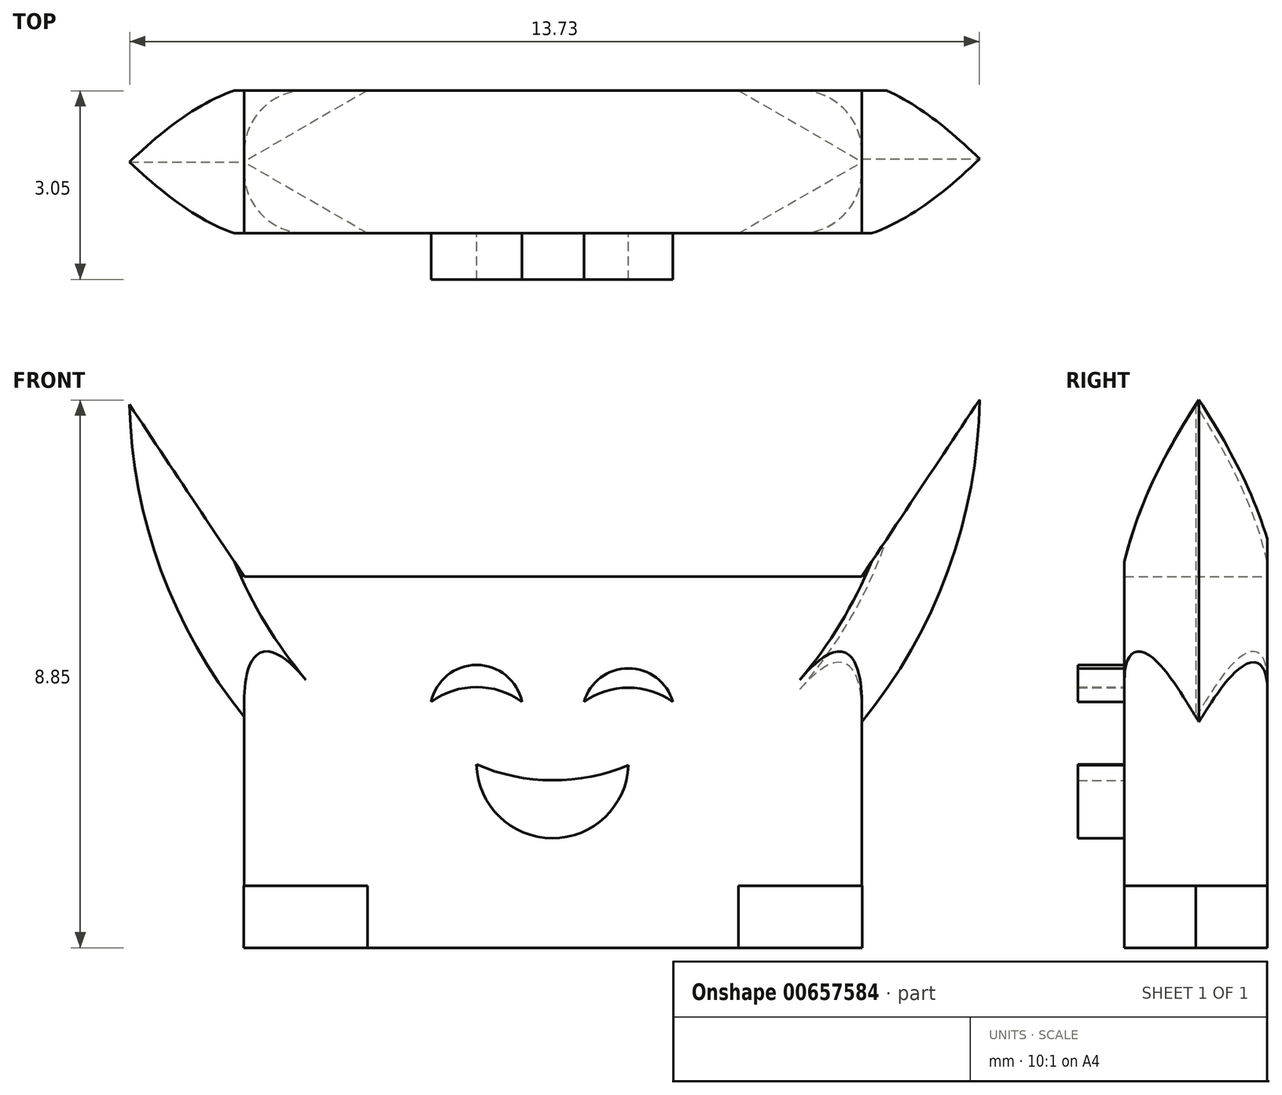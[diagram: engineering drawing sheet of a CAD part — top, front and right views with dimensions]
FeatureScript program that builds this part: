
annotation { "Feature Type Name" : "Feature", "Feature Type Description" : "" }
export const myFeature = defineFeature(function(context is Context, id is Id, definition is map)
    precondition{}
    {
        {
            var Q0;
            Q0=qCreatedBy(makeId("Top.planeOp"),FACE);
            var sketch = newSketch(context, id + "F0", { "sketchPlane" : qUnion([Q0])});
            skLineSegment(sketch, "E0.bottom", {"start": v(-3, -1.15) * mm, "end": v(3, -1.15) * mm});
            skLineSegment(sketch, "E0.top", {"start": v(-3, 1.15) * mm, "end": v(3, 1.15) * mm});
            skPoint(sketch, "E0.middle", {"position": v(0, 0) * mm});
            skLineSegment(sketch, "E1", {"start": v(-3, 1.15) * mm, "end": v(-5, 0) * mm});
            skLineSegment(sketch, "E2", {"start": v(-3, -1.15) * mm, "end": v(-5, 0) * mm});
            skLineSegment(sketch, "E3", {"start": v(3, 1.15) * mm, "end": v(5, 0) * mm});
            skLineSegment(sketch, "E4", {"start": v(3, -1.15) * mm, "end": v(5, 0) * mm});
            skSolve(sketch);
        }
        {
            var Q0;
            Q0 = qSketchRegion(id + "F0", true);
            extrude(context, id + "F1", {"entities" : qUnion([Q0]), "depth" : 1 * mm, "offsetDistance" : 25 * mm});
        }
        {
            var Q0;
            Q0=makeQuery(id+"F1.opExtrude","CAP_FACE",FACE,{"disambiguationData":[OSD([sQuery(id+"F0.wireOp",EDGE,"E0.bottom"),sQuery(id+"F0.wireOp",EDGE,"E0.top"),sQuery(id+"F0.wireOp",EDGE,"E1"),sQuery(id+"F0.wireOp",EDGE,"E2"),sQuery(id+"F0.wireOp",EDGE,"E3"),sQuery(id+"F0.wireOp",EDGE,"E4")])],"isStart":false});
            var sketch = newSketch(context, id + "F2", { "sketchPlane" : qUnion([Q0])});
            skLineSegment(sketch, "E5.bottom", {"start": v(-5, 1.15) * mm, "end": v(5, 1.15) * mm});
            skLineSegment(sketch, "E5.top", {"start": v(-5, -1.15) * mm, "end": v(5, -1.15) * mm});
            skLineSegment(sketch, "E5.left", {"start": v(-5, 1.15) * mm, "end": v(-5, -1.15) * mm});
            skLineSegment(sketch, "E5.right", {"start": v(5, 1.15) * mm, "end": v(5, -1.15) * mm});
            skPoint(sketch, "E5.middle", {"position": v(0, 0) * mm});
            skSolve(sketch);
        }
        {
            var Q0;
            Q0 = qSketchRegion(id + "F2", true);
            extrude(context, id + "F3", {"entities" : qUnion([Q0]), "operationType" : NewBodyOperationType.ADD, "depth" : 5 * mm, "offsetDistance" : 25 * mm});
        }
        {
            var Q0;
            Q0=makeQuery(id+"F3.opExtrude","SWEPT_FACE",FACE,{"disambiguationData":[OSD([sQuery(id+"F2.wireOp",EDGE,"E5.right")])]});
            var sketch = newSketch(context, id + "F4", { "sketchPlane" : qUnion([Q0])});
            skLineSegment(sketch, "E6.bottom", {"start": v(-1.15, 1) * mm, "end": v(1.15, 1) * mm});
            skLineSegment(sketch, "E6.top", {"start": v(-1.15, 3.5) * mm, "end": v(1.15, 3.5) * mm});
            skLineSegment(sketch, "E6.left", {"start": v(-1.15, 1) * mm, "end": v(-1.15, 3.5) * mm});
            skLineSegment(sketch, "E6.right", {"start": v(1.15, 1) * mm, "end": v(1.15, 3.5) * mm});
            skLineSegment(sketch, "E7.top", {"start": v(-1.15, 6) * mm, "end": v(1.15, 6) * mm});
            skLineSegment(sketch, "E7.left", {"start": v(-1.15, 3.5) * mm, "end": v(-1.15, 6) * mm});
            skLineSegment(sketch, "E7.right", {"start": v(1.15, 3.5) * mm, "end": v(1.15, 6) * mm});
            skSolve(sketch);
        }
        {
            var Q0;
            Q0=makeQuery(id+"F4.imprint","IMPRINT",FACE,{"disambiguationData":[TD([[makeQuery(id+"F4.imprint","IMPRINT",EDGE,{"derivedFrom":sQuery(id+"F4.wireOp",EDGE,"E6.top")}),1.0]])]});
            extrude(context, id + "F5", {"entities" : qUnion([Q0]), "operationType" : NewBodyOperationType.ADD, "depth" : 2 * mm, "offsetDistance" : 25 * mm});
        }
        {
            var Q0;
            Q0=makeQuery(id+"F5.boolean.opBoolean","MERGE",FACE,{"derivedFrom":[makeQuery(id+"F3.opExtrude","CAP_FACE",FACE,{"disambiguationData":[OSD([sQuery(id+"F2.wireOp",EDGE,"E5.bottom"),sQuery(id+"F2.wireOp",EDGE,"E5.top"),sQuery(id+"F2.wireOp",EDGE,"E5.left"),sQuery(id+"F2.wireOp",EDGE,"E5.right")])],"isStart":false}),makeQuery(id+"F5.opExtrude","SWEPT_FACE",FACE,{"disambiguationData":[OSD([sQuery(id+"F4.wireOp",EDGE,"E7.top")])]})]});
            var sketch = newSketch(context, id + "F6", { "sketchPlane" : qUnion([Q0])});
            skLineSegment(sketch, "E8.bottom", {"start": v(7, -1.15) * mm, "end": v(5, -1.15) * mm});
            skLineSegment(sketch, "E8.top", {"start": v(7, 1.15) * mm, "end": v(5, 1.15) * mm});
            skLineSegment(sketch, "E8.left", {"start": v(7, -1.15) * mm, "end": v(7, 1.15) * mm});
            skLineSegment(sketch, "E8.right", {"start": v(5, -1.15) * mm, "end": v(5, 1.15) * mm});
            skSolve(sketch);
        }
        {
            var Q0;
            Q0=makeQuery(id+"F6.imprint","IMPRINT",FACE,{"disambiguationData":[TD([[makeQuery(id+"F6.imprint","IMPRINT",EDGE,{"derivedFrom":sQuery(id+"F6.wireOp",EDGE,"E8.bottom")}),1.0]])]});
            extrude(context, id + "F7", {"entities" : qUnion([Q0]), "operationType" : NewBodyOperationType.ADD, "depth" : 3 * mm, "offsetDistance" : 25 * mm});
        }
        {
            var Q0;
            Q0=makeQuery(id+"F5.opExtrude","CAP_EDGE",EDGE,{"disambiguationData":[OSD([sQuery(id+"F4.wireOp",EDGE,"E6.top")])],"isStart":false});
            fillet(context, id + "F8", {"entities" : qUnion([Q0]), "radius" : 8.5 * mm, "tangentPropagation" : true, "allowEdgeOverflow" : false});
        }
        {
            var Q0;
            Q0=makeQuery(id+"F7.opExtrude","CAP_EDGE",EDGE,{"disambiguationData":[OSD([sQuery(id+"F6.wireOp",EDGE,"E8.right")])],"isStart":false});
            chamfer(context, id + "F9", {"entities" : qUnion([Q0]), "chamferType" : ChamferType.TWO_OFFSETS, "width1" : 3 * mm, "oppositeDirection" : false, "width2" : 2 * mm, "tangentPropagation" : true});
        }
        {
            var Q0;
            Q0=makeQuery(id+"F8.opFillet","BLEND_EDGE",EDGE,{"blendedFrom":[makeQuery(id+"F5.opExtrude","CAP_EDGE",EDGE,{"disambiguationData":[OSD([sQuery(id+"F4.wireOp",EDGE,"E6.top")])],"isStart":false}),makeQuery(id+"F7.boolean.opBoolean","MERGE",FACE,{"derivedFrom":[makeQuery(id+"F5.boolean.opBoolean","MERGE",FACE,{"derivedFrom":[makeQuery(id+"F3.boolean.opBoolean","MERGE",FACE,{"derivedFrom":[makeQuery(id+"F1.opExtrude","SWEPT_FACE",FACE,{"disambiguationData":[OSD([sQuery(id+"F0.wireOp",EDGE,"E0.bottom")])]}),makeQuery(id+"F3.opExtrude","SWEPT_FACE",FACE,{"disambiguationData":[OSD([sQuery(id+"F2.wireOp",EDGE,"E5.top")])]})]}),makeQuery(id+"F5.opExtrude","SWEPT_FACE",FACE,{"disambiguationData":[OSD([sQuery(id+"F4.wireOp",EDGE,"E7.left")])]})]}),makeQuery(id+"F7.opExtrude","SWEPT_FACE",FACE,{"disambiguationData":[OSD([sQuery(id+"F6.wireOp",EDGE,"E8.bottom")])]})]})],"blendedInto":[makeQuery(id+"F7.boolean.opBoolean","MERGE",FACE,{"derivedFrom":[makeQuery(id+"F5.boolean.opBoolean","MERGE",FACE,{"derivedFrom":[makeQuery(id+"F3.boolean.opBoolean","MERGE",FACE,{"derivedFrom":[makeQuery(id+"F1.opExtrude","SWEPT_FACE",FACE,{"disambiguationData":[OSD([sQuery(id+"F0.wireOp",EDGE,"E0.bottom")])]}),makeQuery(id+"F3.opExtrude","SWEPT_FACE",FACE,{"disambiguationData":[OSD([sQuery(id+"F2.wireOp",EDGE,"E5.top")])]})]}),makeQuery(id+"F5.opExtrude","SWEPT_FACE",FACE,{"disambiguationData":[OSD([sQuery(id+"F4.wireOp",EDGE,"E7.left")])]})]}),makeQuery(id+"F7.opExtrude","SWEPT_FACE",FACE,{"disambiguationData":[OSD([sQuery(id+"F6.wireOp",EDGE,"E8.bottom")])]})]})]});
            chamfer(context, id + "F10", {"entities" : qUnion([Q0]), "width" : 1.3 * mm, "tangentPropagation" : true});
        }
        {
            var Q0;
            Q0=makeQuery(id+"F8.opFillet","BLEND_EDGE",EDGE,{"blendedFrom":[makeQuery(id+"F5.opExtrude","CAP_EDGE",EDGE,{"disambiguationData":[OSD([sQuery(id+"F4.wireOp",EDGE,"E6.top")])],"isStart":false}),makeQuery(id+"F7.boolean.opBoolean","MERGE",FACE,{"derivedFrom":[makeQuery(id+"F5.boolean.opBoolean","MERGE",FACE,{"derivedFrom":[makeQuery(id+"F3.boolean.opBoolean","MERGE",FACE,{"derivedFrom":[makeQuery(id+"F1.opExtrude","SWEPT_FACE",FACE,{"disambiguationData":[OSD([sQuery(id+"F0.wireOp",EDGE,"E0.top")])]}),makeQuery(id+"F3.opExtrude","SWEPT_FACE",FACE,{"disambiguationData":[OSD([sQuery(id+"F2.wireOp",EDGE,"E5.bottom")])]})]}),makeQuery(id+"F5.opExtrude","SWEPT_FACE",FACE,{"disambiguationData":[OSD([sQuery(id+"F4.wireOp",EDGE,"E7.right")])]})]}),makeQuery(id+"F7.opExtrude","SWEPT_FACE",FACE,{"disambiguationData":[OSD([sQuery(id+"F6.wireOp",EDGE,"E8.top")])]})]})],"blendedInto":[makeQuery(id+"F7.boolean.opBoolean","MERGE",FACE,{"derivedFrom":[makeQuery(id+"F5.boolean.opBoolean","MERGE",FACE,{"derivedFrom":[makeQuery(id+"F3.boolean.opBoolean","MERGE",FACE,{"derivedFrom":[makeQuery(id+"F1.opExtrude","SWEPT_FACE",FACE,{"disambiguationData":[OSD([sQuery(id+"F0.wireOp",EDGE,"E0.top")])]}),makeQuery(id+"F3.opExtrude","SWEPT_FACE",FACE,{"disambiguationData":[OSD([sQuery(id+"F2.wireOp",EDGE,"E5.bottom")])]})]}),makeQuery(id+"F5.opExtrude","SWEPT_FACE",FACE,{"disambiguationData":[OSD([sQuery(id+"F4.wireOp",EDGE,"E7.right")])]})]}),makeQuery(id+"F7.opExtrude","SWEPT_FACE",FACE,{"disambiguationData":[OSD([sQuery(id+"F6.wireOp",EDGE,"E8.top")])]})]})]});
            chamfer(context, id + "F11", {"entities" : qUnion([Q0]), "width" : 1.2 * mm, "tangentPropagation" : true});
        }
        {
            var Q0;
            Q0=makeQuery(id+"F3.opExtrude","SWEPT_EDGE",EDGE,{"disambiguationData":[OSD([sQuery(id+"F2.wireOp",EDGE,"E5.top"),sQuery(id+"F2.wireOp",EDGE,"E5.right")])]});
            fillet(context, id + "F12", {"entities" : qUnion([Q0]), "radius" : 1 * mm, "tangentPropagation" : true, "allowEdgeOverflow" : false});
        }
        {
            var Q0;
            Q0=makeQuery(id+"F3.opExtrude","SWEPT_EDGE",EDGE,{"disambiguationData":[OSD([sQuery(id+"F2.wireOp",EDGE,"E5.bottom"),sQuery(id+"F2.wireOp",EDGE,"E5.right")])]});
            fillet(context, id + "F13", {"entities" : qUnion([Q0]), "radius" : 1 * mm, "tangentPropagation" : true, "allowEdgeOverflow" : false});
        }
        {
            var Q0;
            Q0=makeQuery(id+"F3.opExtrude","SWEPT_FACE",FACE,{"disambiguationData":[OSD([sQuery(id+"F2.wireOp",EDGE,"E5.left")])]});
            var sketch = newSketch(context, id + "F14", { "sketchPlane" : qUnion([Q0])});
            skLineSegment(sketch, "E9.bottom", {"start": v(-1.15, 6) * mm, "end": v(1.15, 6) * mm});
            skLineSegment(sketch, "E9.top", {"start": v(-1.15, 3.5) * mm, "end": v(1.15, 3.5) * mm});
            skLineSegment(sketch, "E9.left", {"start": v(-1.15, 6) * mm, "end": v(-1.15, 3.5) * mm});
            skLineSegment(sketch, "E9.right", {"start": v(1.15, 6) * mm, "end": v(1.15, 3.5) * mm});
            skSolve(sketch);
        }
        {
            var Q0;
            Q0 = qSketchRegion(id + "F14", true);
            extrude(context, id + "F15", {"entities" : qUnion([Q0]), "operationType" : NewBodyOperationType.ADD, "depth" : 2 * mm, "offsetDistance" : 25 * mm});
        }
        {
            var Q0;
            Q0=makeQuery(id+"F15.boolean.opBoolean","MERGE",FACE,{"derivedFrom":[makeQuery(id+"F5.boolean.opBoolean","MERGE",FACE,{"derivedFrom":[makeQuery(id+"F3.opExtrude","CAP_FACE",FACE,{"disambiguationData":[OSD([sQuery(id+"F2.wireOp",EDGE,"E5.bottom"),sQuery(id+"F2.wireOp",EDGE,"E5.top"),sQuery(id+"F2.wireOp",EDGE,"E5.left"),sQuery(id+"F2.wireOp",EDGE,"E5.right")])],"isStart":false}),makeQuery(id+"F5.opExtrude","SWEPT_FACE",FACE,{"disambiguationData":[OSD([sQuery(id+"F4.wireOp",EDGE,"E7.top")])]})]}),makeQuery(id+"F15.opExtrude","SWEPT_FACE",FACE,{"disambiguationData":[OSD([sQuery(id+"F14.wireOp",EDGE,"E9.bottom")])]})]});
            var sketch = newSketch(context, id + "F16", { "sketchPlane" : qUnion([Q0])});
            skLineSegment(sketch, "E10.bottom", {"start": v(-7, -1.15) * mm, "end": v(-5, -1.15) * mm});
            skLineSegment(sketch, "E10.top", {"start": v(-7, 1.15) * mm, "end": v(-5, 1.15) * mm});
            skLineSegment(sketch, "E10.left", {"start": v(-7, -1.15) * mm, "end": v(-7, 1.15) * mm});
            skLineSegment(sketch, "E10.right", {"start": v(-5, -1.15) * mm, "end": v(-5, 1.15) * mm});
            skSolve(sketch);
        }
        {
            var Q0;
            Q0=makeQuery(id+"F16.imprint","IMPRINT",FACE,{"disambiguationData":[TD([[makeQuery(id+"F16.imprint","IMPRINT",EDGE,{"derivedFrom":sQuery(id+"F16.wireOp",EDGE,"E10.bottom")}),1.0]])]});
            extrude(context, id + "F17", {"entities" : qUnion([Q0]), "operationType" : NewBodyOperationType.ADD, "depth" : 3 * mm, "offsetDistance" : 25 * mm});
        }
        {
            var Q0;
            Q0=makeQuery(id+"F15.opExtrude","CAP_EDGE",EDGE,{"disambiguationData":[OSD([sQuery(id+"F14.wireOp",EDGE,"E9.top")])],"isStart":false});
            fillet(context, id + "F18", {"entities" : qUnion([Q0]), "radius" : 8.5 * mm, "tangentPropagation" : true, "allowEdgeOverflow" : false});
        }
        {
            var Q0;
            Q0=makeQuery(id+"F17.opExtrude","CAP_EDGE",EDGE,{"disambiguationData":[OSD([sQuery(id+"F16.wireOp",EDGE,"E10.right")])],"isStart":false});
            chamfer(context, id + "F19", {"entities" : qUnion([Q0]), "chamferType" : ChamferType.TWO_OFFSETS, "width1" : 2 * mm, "oppositeDirection" : false, "width2" : 3 * mm, "tangentPropagation" : true});
        }
        {
            var Q0;
            Q0=makeQuery(id+"F18.opFillet","BLEND_EDGE",EDGE,{"blendedFrom":[makeQuery(id+"F15.opExtrude","CAP_EDGE",EDGE,{"disambiguationData":[OSD([sQuery(id+"F14.wireOp",EDGE,"E9.top")])],"isStart":false}),makeQuery(id+"F17.boolean.opBoolean","MERGE",FACE,{"derivedFrom":[makeQuery(id+"F15.boolean.opBoolean","MERGE",FACE,{"derivedFrom":[makeQuery(id+"F7.boolean.opBoolean","MERGE",FACE,{"derivedFrom":[makeQuery(id+"F5.boolean.opBoolean","MERGE",FACE,{"derivedFrom":[makeQuery(id+"F3.boolean.opBoolean","MERGE",FACE,{"derivedFrom":[makeQuery(id+"F1.opExtrude","SWEPT_FACE",FACE,{"disambiguationData":[OSD([sQuery(id+"F0.wireOp",EDGE,"E0.bottom")])]}),makeQuery(id+"F3.opExtrude","SWEPT_FACE",FACE,{"disambiguationData":[OSD([sQuery(id+"F2.wireOp",EDGE,"E5.top")])]})]}),makeQuery(id+"F5.opExtrude","SWEPT_FACE",FACE,{"disambiguationData":[OSD([sQuery(id+"F4.wireOp",EDGE,"E7.left")])]})]}),makeQuery(id+"F7.opExtrude","SWEPT_FACE",FACE,{"disambiguationData":[OSD([sQuery(id+"F6.wireOp",EDGE,"E8.bottom")])]})]}),makeQuery(id+"F15.opExtrude","SWEPT_FACE",FACE,{"disambiguationData":[OSD([sQuery(id+"F14.wireOp",EDGE,"E9.right")])]})]}),makeQuery(id+"F17.opExtrude","SWEPT_FACE",FACE,{"disambiguationData":[OSD([sQuery(id+"F16.wireOp",EDGE,"E10.bottom")])]})]})],"blendedInto":[makeQuery(id+"F17.boolean.opBoolean","MERGE",FACE,{"derivedFrom":[makeQuery(id+"F15.boolean.opBoolean","MERGE",FACE,{"derivedFrom":[makeQuery(id+"F7.boolean.opBoolean","MERGE",FACE,{"derivedFrom":[makeQuery(id+"F5.boolean.opBoolean","MERGE",FACE,{"derivedFrom":[makeQuery(id+"F3.boolean.opBoolean","MERGE",FACE,{"derivedFrom":[makeQuery(id+"F1.opExtrude","SWEPT_FACE",FACE,{"disambiguationData":[OSD([sQuery(id+"F0.wireOp",EDGE,"E0.bottom")])]}),makeQuery(id+"F3.opExtrude","SWEPT_FACE",FACE,{"disambiguationData":[OSD([sQuery(id+"F2.wireOp",EDGE,"E5.top")])]})]}),makeQuery(id+"F5.opExtrude","SWEPT_FACE",FACE,{"disambiguationData":[OSD([sQuery(id+"F4.wireOp",EDGE,"E7.left")])]})]}),makeQuery(id+"F7.opExtrude","SWEPT_FACE",FACE,{"disambiguationData":[OSD([sQuery(id+"F6.wireOp",EDGE,"E8.bottom")])]})]}),makeQuery(id+"F15.opExtrude","SWEPT_FACE",FACE,{"disambiguationData":[OSD([sQuery(id+"F14.wireOp",EDGE,"E9.right")])]})]}),makeQuery(id+"F17.opExtrude","SWEPT_FACE",FACE,{"disambiguationData":[OSD([sQuery(id+"F16.wireOp",EDGE,"E10.bottom")])]})]})]});
            chamfer(context, id + "F20", {"entities" : qUnion([Q0]), "width" : 1.3 * mm, "tangentPropagation" : true});
        }
        {
            var Q0;
            Q0=makeQuery(id+"F18.opFillet","BLEND_EDGE",EDGE,{"blendedFrom":[makeQuery(id+"F15.opExtrude","CAP_EDGE",EDGE,{"disambiguationData":[OSD([sQuery(id+"F14.wireOp",EDGE,"E9.top")])],"isStart":false}),makeQuery(id+"F17.boolean.opBoolean","MERGE",FACE,{"derivedFrom":[makeQuery(id+"F15.boolean.opBoolean","MERGE",FACE,{"derivedFrom":[makeQuery(id+"F7.boolean.opBoolean","MERGE",FACE,{"derivedFrom":[makeQuery(id+"F5.boolean.opBoolean","MERGE",FACE,{"derivedFrom":[makeQuery(id+"F3.boolean.opBoolean","MERGE",FACE,{"derivedFrom":[makeQuery(id+"F1.opExtrude","SWEPT_FACE",FACE,{"disambiguationData":[OSD([sQuery(id+"F0.wireOp",EDGE,"E0.top")])]}),makeQuery(id+"F3.opExtrude","SWEPT_FACE",FACE,{"disambiguationData":[OSD([sQuery(id+"F2.wireOp",EDGE,"E5.bottom")])]})]}),makeQuery(id+"F5.opExtrude","SWEPT_FACE",FACE,{"disambiguationData":[OSD([sQuery(id+"F4.wireOp",EDGE,"E7.right")])]})]}),makeQuery(id+"F7.opExtrude","SWEPT_FACE",FACE,{"disambiguationData":[OSD([sQuery(id+"F6.wireOp",EDGE,"E8.top")])]})]}),makeQuery(id+"F15.opExtrude","SWEPT_FACE",FACE,{"disambiguationData":[OSD([sQuery(id+"F14.wireOp",EDGE,"E9.left")])]})]}),makeQuery(id+"F17.opExtrude","SWEPT_FACE",FACE,{"disambiguationData":[OSD([sQuery(id+"F16.wireOp",EDGE,"E10.top")])]})]})],"blendedInto":[makeQuery(id+"F17.boolean.opBoolean","MERGE",FACE,{"derivedFrom":[makeQuery(id+"F15.boolean.opBoolean","MERGE",FACE,{"derivedFrom":[makeQuery(id+"F7.boolean.opBoolean","MERGE",FACE,{"derivedFrom":[makeQuery(id+"F5.boolean.opBoolean","MERGE",FACE,{"derivedFrom":[makeQuery(id+"F3.boolean.opBoolean","MERGE",FACE,{"derivedFrom":[makeQuery(id+"F1.opExtrude","SWEPT_FACE",FACE,{"disambiguationData":[OSD([sQuery(id+"F0.wireOp",EDGE,"E0.top")])]}),makeQuery(id+"F3.opExtrude","SWEPT_FACE",FACE,{"disambiguationData":[OSD([sQuery(id+"F2.wireOp",EDGE,"E5.bottom")])]})]}),makeQuery(id+"F5.opExtrude","SWEPT_FACE",FACE,{"disambiguationData":[OSD([sQuery(id+"F4.wireOp",EDGE,"E7.right")])]})]}),makeQuery(id+"F7.opExtrude","SWEPT_FACE",FACE,{"disambiguationData":[OSD([sQuery(id+"F6.wireOp",EDGE,"E8.top")])]})]}),makeQuery(id+"F15.opExtrude","SWEPT_FACE",FACE,{"disambiguationData":[OSD([sQuery(id+"F14.wireOp",EDGE,"E9.left")])]})]}),makeQuery(id+"F17.opExtrude","SWEPT_FACE",FACE,{"disambiguationData":[OSD([sQuery(id+"F16.wireOp",EDGE,"E10.top")])]})]})]});
            chamfer(context, id + "F21", {"entities" : qUnion([Q0]), "width" : 1.3 * mm, "tangentPropagation" : true});
        }
        {
            var Q0;
            Q0=makeQuery(id+"F3.opExtrude","SWEPT_EDGE",EDGE,{"disambiguationData":[OSD([sQuery(id+"F2.wireOp",EDGE,"E5.bottom"),sQuery(id+"F2.wireOp",EDGE,"E5.left")])]});
            fillet(context, id + "F22", {"entities" : qUnion([Q0]), "radius" : 1 * mm, "tangentPropagation" : true, "allowEdgeOverflow" : false});
        }
        {
            var Q0;
            Q0=makeQuery(id+"F3.opExtrude","SWEPT_EDGE",EDGE,{"disambiguationData":[OSD([sQuery(id+"F2.wireOp",EDGE,"E5.top"),sQuery(id+"F2.wireOp",EDGE,"E5.left")])]});
            fillet(context, id + "F23", {"entities" : qUnion([Q0]), "radius" : 1 * mm, "tangentPropagation" : true, "allowEdgeOverflow" : false});
        }
        {
            var Q0;
            Q0=makeQuery(id+"F17.boolean.opBoolean","MERGE",FACE,{"derivedFrom":[makeQuery(id+"F15.boolean.opBoolean","MERGE",FACE,{"derivedFrom":[makeQuery(id+"F7.boolean.opBoolean","MERGE",FACE,{"derivedFrom":[makeQuery(id+"F5.boolean.opBoolean","MERGE",FACE,{"derivedFrom":[makeQuery(id+"F3.boolean.opBoolean","MERGE",FACE,{"derivedFrom":[makeQuery(id+"F1.opExtrude","SWEPT_FACE",FACE,{"disambiguationData":[OSD([sQuery(id+"F0.wireOp",EDGE,"E0.bottom")])]}),makeQuery(id+"F3.opExtrude","SWEPT_FACE",FACE,{"disambiguationData":[OSD([sQuery(id+"F2.wireOp",EDGE,"E5.top")])]})]}),makeQuery(id+"F5.opExtrude","SWEPT_FACE",FACE,{"disambiguationData":[OSD([sQuery(id+"F4.wireOp",EDGE,"E7.left")])]})]}),makeQuery(id+"F7.opExtrude","SWEPT_FACE",FACE,{"disambiguationData":[OSD([sQuery(id+"F6.wireOp",EDGE,"E8.bottom")])]})]}),makeQuery(id+"F15.opExtrude","SWEPT_FACE",FACE,{"disambiguationData":[OSD([sQuery(id+"F14.wireOp",EDGE,"E9.right")])]})]}),makeQuery(id+"F17.opExtrude","SWEPT_FACE",FACE,{"disambiguationData":[OSD([sQuery(id+"F16.wireOp",EDGE,"E10.bottom")])]})]});
            var sketch = newSketch(context, id + "F24", { "sketchPlane" : qUnion([Q0])});
            skArc(sketch, "E11", {"start": v(-0.5, 3.97) * mm, "mid": v(-1.23, 4.21) * mm, "end": v(-1.97, 3.97) * mm});
            skArc(sketch, "E12", {"start": v(1.94, 3.97) * mm, "mid": v(1.22, 4.2) * mm, "end": v(0.5, 3.97) * mm});
            skArc(sketch, "E13", {"start": v(-0.5, 3.97) * mm, "mid": v(-1.23, 4.57) * mm, "end": v(-1.97, 3.97) * mm});
            skArc(sketch, "E14", {"start": v(1.94, 3.97) * mm, "mid": v(1.22, 4.51) * mm, "end": v(0.5, 3.97) * mm});
            skArc(sketch, "E15", {"start": v(-1.23, 2.96) * mm, "mid": v(0, 2.7) * mm, "end": v(1.22, 2.95) * mm});
            skArc(sketch, "E16", {"start": v(-1.23, 2.96) * mm, "mid": v(-0.01, 1.77) * mm, "end": v(1.22, 2.95) * mm});
            skSolve(sketch);
        }
        {
            var Q0;
            Q0=makeQuery(id+"F24.imprint","IMPRINT",FACE,{"disambiguationData":[TD([[makeQuery(id+"F24.imprint","IMPRINT",EDGE,{"derivedFrom":sQuery(id+"F24.wireOp",EDGE,"E15")}),-1.0]])]});
            var Q1;
            Q1=makeQuery(id+"F24.imprint","IMPRINT",FACE,{"disambiguationData":[TD([[makeQuery(id+"F24.imprint","IMPRINT",EDGE,{"derivedFrom":sQuery(id+"F24.wireOp",EDGE,"E12")}),-1.0]])]});
            var Q2;
            Q2=makeQuery(id+"F24.imprint","IMPRINT",FACE,{"disambiguationData":[TD([[makeQuery(id+"F24.imprint","IMPRINT",EDGE,{"derivedFrom":sQuery(id+"F24.wireOp",EDGE,"E11")}),-1.0]])]});
            extrude(context, id + "F25", {"entities" : qUnion([Q0, Q1, Q2]), "operationType" : NewBodyOperationType.ADD, "depth" : .75 * mm, "offsetDistance" : 25 * mm});
        }
    });
